# Revit family: TCNHBLE_with_Mixing_Box
name_source: partatom
category: Mechanical Equipment
units: mm (PartAtom-declared; Revit-internal decimal feet)

## family parameters
Always vertical = Yes
Cut with Voids When Loaded = No
Part Type = Normal
Room Calculation Point = No
Round Connector Dimension = Use Diameter
Shared = No
Work Plane-Based = No

## types (17) — shared parameters
0 = 0' - 0"
1" = 0' - 1"
1.5 = 0' - 1 1/2"
135 = 135.00°
2" = 0' - 2"
2' = 2' - 0"
3" = 0' - 3"
3.125" = 0' - 3 1/8"
4" = 0' - 4"
5" = 0' - 5"
Manufacturer = Loren Cook Company
Model = TCNHBLE-Mixing Box
ONE EIGTH = 0' - 0 1/8"
Type Comments = Tubular Centrifugal Inline Upblast Roof Mounted Arrangement 9 With Mixing Box
URL = www.lorencook.com

## per-type parameters (varying)
| type | ((E-8")*.8)-MIXING_BOX | (E/2)+.125" | -B/2 | A | A-C-D | B | B/2 | C | C/2 | D | E | F | F-1" | FAN_DIA | FAN_RAD | FAN_RAD*.33 | FAN_RAD*.8 | FAN_RAD+4" | MB/2 | MIXING_BOX_HEIGHT | MIXING_BOX_HEIGHT+.125" | MIXING_BOX_HEIGHT-2.875" | RO | RO/2 |
| 100_TCNHBLE_with_Mixing_Box | -1' - 7 19/32" | 1' - 0 1/8" | -0' - 11 17/32" | 10' - 0" | 3' - 5" | 1' - 11 1/16" | 0' - 11 17/32" | 2' - 0" | 2' - 6" | 2' - 10" | 5' - 0" | 1' - 8" | 1' - 7" | 1' - 4" | 0' - 8" | 0' - 5 9/32" | 0' - 4 13/16" | 1' - 0" | 1' - 3 1/4" | 2' - 6 1/2" | 2' - 6 5/8" | 2' - 3 5/8" | 1' - 4 13/16" | 0' - 8 13/32" |
| 120_TCNHBLE_with_Mixing_Box | -1' - 8 13/32" | 1' - 2 1/8" | -1' - 1 17/32" | 10' - 0" | 3' - 1" | 2' - 3 1/16" | 1' - 1 17/32" | 2' - 4" | 2' - 7" | 3' - 2" | 5' - 2" | 1' - 10" | 1' - 9" | 1' - 6" | 0' - 9" | 0' - 5 15/16" | 0' - 5 13/32" | 1' - 1" | 1' - 3 3/4" | 2' - 7 1/2" | 2' - 7 5/8" | 2' - 4 5/8" | 1' - 8 13/16" | 0' - 10 13/32" |
| 135_TCNHBLE_with_Mixing_Box | -1' - 9" | 1' - 3 1/8" | -1' - 2 1/2" | 10' - 0" | 2' - 8" | 2' - 5" | 1' - 2 1/2" | 2' - 6" | 2' - 7 1/2" | 3' - 4" | 5' - 3" | 2' - 2" | 2' - 1" | 1' - 9" | 0' - 10 1/2" | 0' - 6 15/16" | 0' - 6 5/16" | 1' - 2 1/2" | 1' - 3 7/8" | 2' - 7 3/4" | 2' - 7 7/8" | 2' - 4 7/8" | 1' - 10 3/4" | 0' - 11 3/8" |
| 150_TCNHBLE_with_Mixing_Box | -1' - 11 19/32" | 1' - 4 1/8" | -1' - 3 1/2" | 10' - 0" | 2' - 1" | 2' - 7" | 1' - 3 1/2" | 2' - 8" | 2' - 9 1/2" | 3' - 6" | 5' - 7" | 2' - 5" | 2' - 4" | 2' - 0" | 1' - 0" | 0' - 7 29/32" | 0' - 7 3/16" | 1' - 4" | 1' - 4 1/4" | 2' - 8 1/2" | 2' - 8 5/8" | 2' - 5 5/8" | 2' - 0 3/4" | 1' - 0 3/8" |
| 165_TCNHBLE_with_Mixing_Box | -2' - 0 13/16" | 1' - 5 1/8" | -1' - 4 1/2" | 10' - 0" | 1' - 9" | 2' - 9" | 1' - 4 1/2" | 2' - 10" | 2' - 11" | 3' - 10" | 5' - 10" | 2' - 6" | 2' - 5" | 2' - 2" | 1' - 1" | 0' - 8 19/32" | 0' - 7 13/16" | 1' - 5" | 1' - 5" | 2' - 10" | 2' - 10 1/8" | 2' - 7 1/8" | 2' - 2 3/4" | 1' - 1 3/8" |
| 180_TCNHBLE_with_Mixing_Box | -2' - 2 13/32" | 1' - 7 1/8" | -1' - 6 7/16" | 10' - 0" | 1' - 1" | 3' - 0 7/8" | 1' - 6 7/16" | 3' - 2" | 3' - 0 1/2" | 4' - 2" | 6' - 1" | 2' - 11" | 2' - 10" | 2' - 4" | 1' - 2" | 0' - 9 1/4" | 0' - 8 13/32" | 1' - 6" | 1' - 5 1/2" | 2' - 11" | 2' - 11 1/8" | 2' - 8 1/8" | 2' - 6 5/8" | 1' - 3 5/16" |
| 195_TCNHBLE_with_Mixing_Box | -2' - 4 3/16" | 1' - 9 1/8" | -1' - 8 7/16" | 10' - 0" | 0' - 6" | 3' - 4 7/8" | 1' - 8 7/16" | 3' - 6" | 3' - 2" | 4' - 6" | 6' - 4" | 3' - 3" | 3' - 2" | 2' - 7" | 1' - 3 1/2" | 0' - 10 7/32" | 0' - 9 5/16" | 1' - 7 1/2" | 1' - 5 7/8" | 2' - 11 3/4" | 2' - 11 7/8" | 2' - 8 7/8" | 2' - 10 11/16" | 1' - 5 11/32" |
| 210_TCNHBLE_with_Mixing_Box | -2' - 5 3/16" | 1' - 10 1/8" | -1' - 9 7/16" | 10' - 4" | 0' - 7" | 3' - 6 7/8" | 1' - 9 7/16" | 3' - 8" | 3' - 2" | 4' - 8" | 6' - 4" | 3' - 6" | 3' - 5" | 2' - 10" | 1' - 5" | 0' - 11 7/32" | 0' - 10 3/16" | 1' - 9" | 1' - 5 1/4" | 2' - 10 1/2" | 2' - 10 5/8" | 2' - 7 5/8" | 3' - 0 11/16" | 1' - 6 11/32" |
| 225_TCNHBLE_with_Mixing_Box | -2' - 6 3/16" | 2' - 0 1/8" | -1' - 11 7/16" | 10' - 1 1/2" | 0' - 0 1/2" | 3' - 10 7/8" | 1' - 11 7/16" | 4' - 0" | 3' - 3" | 5' - 0" | 6' - 6" | 3' - 8" | 3' - 7" | 3' - 0" | 1' - 6" | 0' - 11 7/8" | 0' - 10 13/16" | 1' - 10" | 1' - 5 5/8" | 2' - 11 1/4" | 2' - 11 3/8" | 2' - 8 3/8" | 3' - 4 11/16" | 1' - 8 11/32" |
| 245_TCNHBLE_with_Mixing_Box | -2' - 10" | 2' - 1 1/8" | -2' - 0 7/16" | 11' - 3" | 0' - 1" | 4' - 0 7/8" | 2' - 0 7/16" | 4' - 2" | 3' - 6 1/2" | 5' - 3" | 7' - 1" | 4' - 2" | 4' - 1" | 3' - 4" | 1' - 8" | 1' - 1 3/16" | 1' - 0" | 2' - 0" | 1' - 6 3/4" | 3' - 1 1/2" | 3' - 1 5/8" | 2' - 10 5/8" | 3' - 6 11/16" | 1' - 9 11/32" |
| 270_TCNHBLE_with_Mixing_Box | -3' - 2 13/16" | 2' - 3 1/8" | -2' - 2 7/16" | 12' - 2 3/4" | 0' - 0 3/4" | 4' - 4 7/8" | 2' - 2 7/16" | 4' - 6" | 3' - 9 1/2" | 5' - 7" | 7' - 7" | 4' - 8" | 4' - 7" | 3' - 8" | 1' - 10" | 1' - 2 17/32" | 1' - 1 3/16" | 2' - 2" | 1' - 6 3/4" | 3' - 1 1/2" | 3' - 1 5/8" | 2' - 10 5/8" | 3' - 10 11/16" | 1' - 11 11/32" |
| 300_TCNHBLE_with_Mixing_Box | -3' - 3 13/16" | 2' - 6 1/8" | -2' - 5 7/16" | 12' - 9" | 0' - 1" | 4' - 10 7/8" | 2' - 5 7/16" | 5' - 0" | 3' - 10 1/2" | 6' - 2" | 7' - 9" | 5' - 0" | 4' - 11" | 4' - 0" | 2' - 0" | 1' - 3 27/32" | 1' - 2 13/32" | 2' - 4" | 1' - 7 1/8" | 3' - 2 1/4" | 3' - 2 3/8" | 2' - 11 3/8" | 4' - 4 11/16" | 2' - 2 11/32" |
| 330_TCNHBLE_with_Mixing_Box | -3' - 6 13/16" | 2' - 7 1/8" | -2' - 6 3/8" | 13' - 8 1/4" | 0' - 1 1/4" | 5' - 0 3/4" | 2' - 6 3/8" | 5' - 2" | 4' - 2" | 6' - 5" | 8' - 4" | 5' - 4" | 5' - 3" | 4' - 4" | 2' - 2" | 1' - 5 5/32" | 1' - 3 19/32" | 2' - 6" | 1' - 8 3/4" | 3' - 5 1/2" | 3' - 5 5/8" | 3' - 2 5/8" | 4' - 6 9/16" | 2' - 3 9/32" |
| 365_TCNHBLE_with_Mixing_Box | -3' - 8 19/32" | 2' - 8 5/8" | -2' - 7 7/8" | 14' - 2" | 0' - 1" | 5' - 3 3/4" | 2' - 7 7/8" | 5' - 5" | 4' - 4 1/2" | 6' - 10" | 8' - 9" | 5' - 5" | 5' - 4" | 4' - 6" | 2' - 3" | 1' - 5 13/16" | 1' - 4 3/16" | 2' - 7" | 1' - 10 1/8" | 3' - 8 1/4" | 3' - 8 3/8" | 3' - 5 3/8" | 4' - 9 9/16" | 2' - 4 25/32" |
| 402_TCNHBLE_with_Mixing_Box | -4' - 1 3/16" | 3' - 0 1/8" | -2' - 11 3/8" | 15' - 4 3/4" | 0' - 0 3/4" | 5' - 10 3/4" | 2' - 11 3/8" | 6' - 0" | 4' - 8 1/2" | 7' - 6" | 9' - 5" | 6' - 0" | 5' - 11" | 5' - 0" | 2' - 6" | 1' - 7 13/16" | 1' - 6" | 2' - 10" | 1' - 11 1/4" | 3' - 10 1/2" | 3' - 10 5/8" | 3' - 7 5/8" | 5' - 4 9/16" | 2' - 8 9/32" |
| 445_TCNHBLE_with_Mixing_Box | -4' - 6 3/16" | 3' - 2 5/8" | -3' - 1 7/8" | 17' - 2" | 0' - 1" | 6' - 3 3/4" | 3' - 1 7/8" | 6' - 5" | 5' - 3" | 8' - 2" | 10' - 6" | 6' - 8" | 6' - 7" | 5' - 6" | 2' - 9" | 1' - 9 25/32" | 1' - 7 13/16" | 3' - 1" | 2' - 2 5/8" | 4' - 5 1/4" | 4' - 5 3/8" | 4' - 2 3/8" | 5' - 9 9/16" | 2' - 10 25/32" |
| 490_TCNHBLE_with_Mixing_Box | -4' - 11 13/16" | 3' - 6 1/8" | -3' - 5 3/8" | 18' - 9 1/2" | 0' - 0 1/2" | 6' - 10 3/4" | 3' - 5 3/8" | 7' - 0" | 5' - 9 1/2" | 9' - 0" | 11' - 7" | 7' - 3" | 7' - 2" | 6' - 1" | 3' - 0 1/2" | 2' - 0 3/32" | 1' - 9 29/32" | 3' - 4 1/2" | 2' - 5 5/8" | 4' - 11 1/4" | 4' - 11 3/8" | 4' - 8 3/8" | 6' - 4 1/2" | 3' - 2 1/4" |
